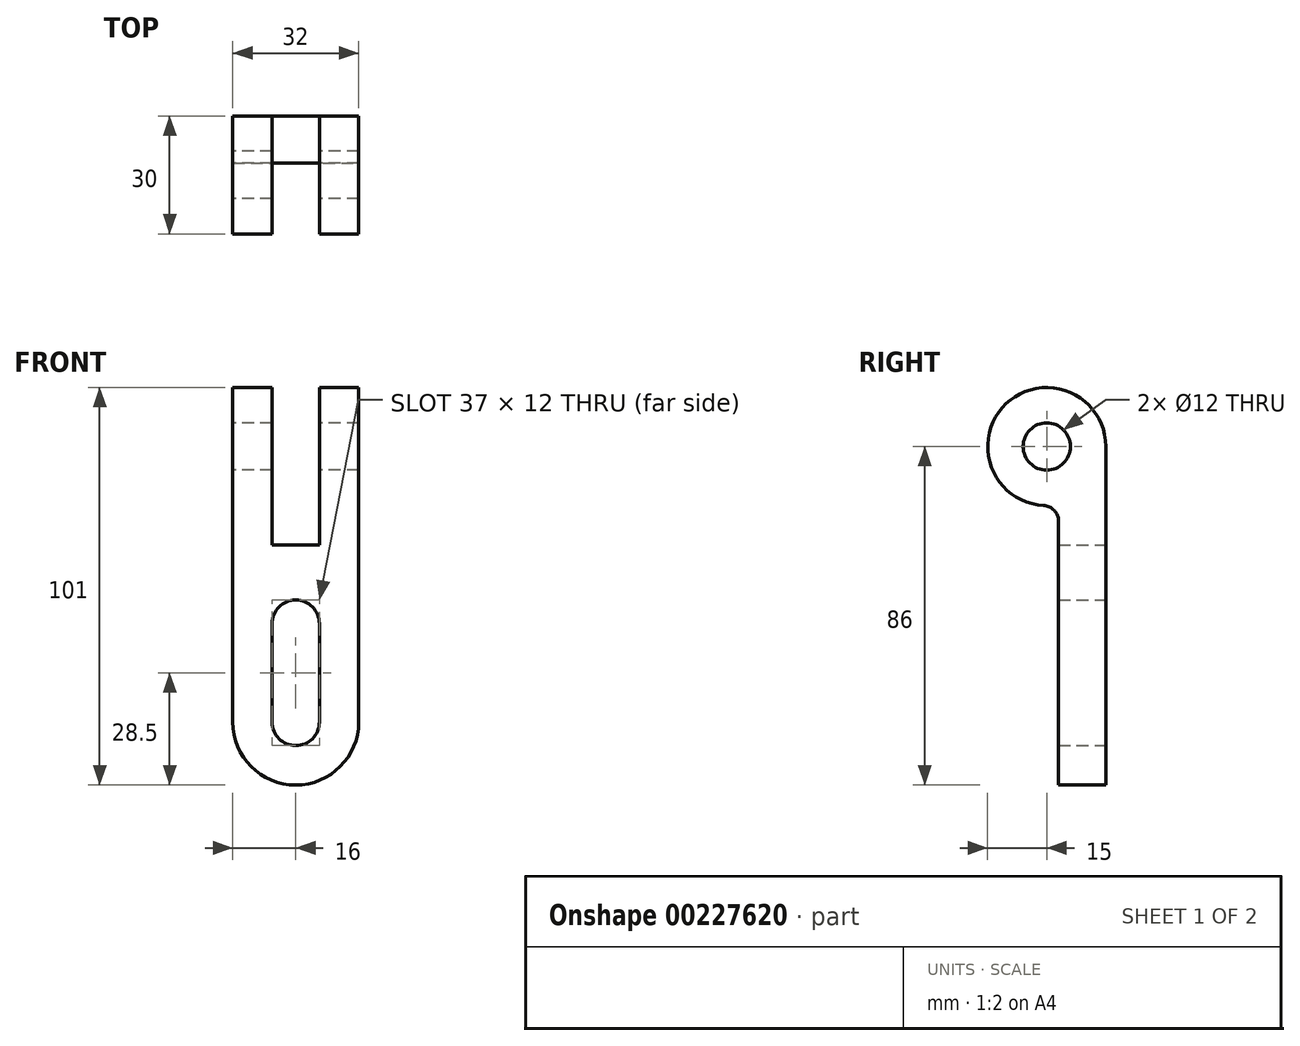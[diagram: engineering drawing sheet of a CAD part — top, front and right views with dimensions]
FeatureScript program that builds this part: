
annotation { "Feature Type Name" : "Feature", "Feature Type Description" : "" }
export const myFeature = defineFeature(function(context is Context, id is Id, definition is map)
    precondition{}
    {
        {
            var Q0;
            Q0=qCreatedBy(makeId("Right.planeOp"),FACE);
            var sketch = newSketch(context, id + "F0", { "sketchPlane" : qUnion([Q0])});
            skCircle(sketch, "E0", {"center": v(0, 0) * mm, "radius": 6 * mm});
            skArc(sketch, "E1", {"start": v(15, 0) * mm, "mid": v(-10.32, 10.88) * mm, "end": v(-0.79, -14.98) * mm});
            skLineSegment(sketch, "E2", {"start": v(3, -86) * mm, "end": v(15, -86) * mm});
            skLineSegment(sketch, "E3", {"start": v(15, -86) * mm, "end": v(15, 0) * mm});
            skLineSegment(sketch, "E4", {"start": v(3, -86) * mm, "end": v(3, -18.97) * mm});
            skPoint(sketch, "E5.visualSharp", {"position": v(3, -14.7) * mm});
            skArc(sketch, "E5.filletArc", {"start": v(3, -18.97) * mm, "mid": v(1.9, -16.22) * mm, "end": v(-0.79, -14.98) * mm});
            skSolve(sketch);
        }
        {
            var Q0;
            Q0 = qSketchRegion(id + "F0", true);
            extrude(context, id + "F1", {"entities" : qUnion([Q0]), "depth" : 16 * mm, "hasSecondDirection" : true, "secondDirectionOppositeDirection" : true, "secondDirectionDepth" : 16 * mm});
        }
        {
            var Q0;
            Q0=makeQuery(id+"F1.opExtrude","SWEPT_FACE",FACE,{"disambiguationData":[OSD([sQuery(id+"F0.wireOp",EDGE,"E3")])]});
            var sketch = newSketch(context, id + "F2", { "sketchPlane" : qUnion([Q0])});
            skLineSegment(sketch, "E6.bottom", {"start": v(-6, 18.67) * mm, "end": v(6, 18.67) * mm});
            skLineSegment(sketch, "E6.top", {"start": v(-6, -25) * mm, "end": v(6, -25) * mm});
            skLineSegment(sketch, "E6.left", {"start": v(-6, 18.67) * mm, "end": v(-6, -25) * mm});
            skLineSegment(sketch, "E6.right", {"start": v(6, 18.67) * mm, "end": v(6, -25) * mm});
            skLineSegment(sketch, "E7", {"start": v(-32.92, -70) * mm, "end": v(42.7, -70) * mm, "construction": true});
            skArc(sketch, "E8", {"start": v(6, -45) * mm, "mid": v(0, -39) * mm, "end": v(-6, -45) * mm});
            skArc(sketch, "E9", {"start": v(-6, -70) * mm, "mid": v(0, -76) * mm, "end": v(6, -70) * mm});
            skArc(sketch, "E10", {"start": v(-16, -70) * mm, "mid": v(0, -86) * mm, "end": v(16, -70) * mm});
            skLineSegment(sketch, "E11", {"start": v(-6, -45) * mm, "end": v(-6, -70) * mm});
            skLineSegment(sketch, "E12", {"start": v(6, -45) * mm, "end": v(6, -70) * mm});
            skSolve(sketch);
        }
        {
            var Q0;
            Q0 = qSketchRegion(id + "F2", true);
            var Q1;
            {var subQ0=sQuery(id+"F2.wireOp",EDGE,"E10");var subQ1=sQuery(id+"F0.wireOp",EDGE,"E3");var subQ2=makeQuery(id+"F1.opExtrude","CAP_EDGE",EDGE,{"disambiguationData":[OSD([subQ1])],"isStart":false});var subQ3=makeQuery(id+"F2.imprint","INTERSECT",VERTEX,{"derivedFrom":[subQ2,subQ0]});Q1=makeQuery(id+"F2.imprint","IMPRINT",FACE,{"disambiguationData":[TD([[makeQuery(id+"F2.imprint","IMPRINT",EDGE,{"disambiguationData":[TD([[subQ3,-1.0]])],"derivedFrom":subQ0}),-1.0]])]});}
            var Q2;
            {var subQ0=sQuery(id+"F2.wireOp",EDGE,"E10");var subQ1=sQuery(id+"F0.wireOp",EDGE,"E3");var subQ2=makeQuery(id+"F1.opExtrude","CAP_EDGE",EDGE,{"disambiguationData":[OSD([subQ1])],"isStart":true});var subQ3=makeQuery(id+"F2.imprint","INTERSECT",VERTEX,{"derivedFrom":[subQ2,subQ0]});Q2=makeQuery(id+"F2.imprint","IMPRINT",FACE,{"disambiguationData":[TD([[makeQuery(id+"F2.imprint","IMPRINT",EDGE,{"disambiguationData":[TD([[subQ3,1.0]])],"derivedFrom":subQ0}),-1.0]])]});}
            extrude(context, id + "F3", {"entities" : qUnion([Q0, Q1, Q2]), "operationType" : NewBodyOperationType.REMOVE, "endBound" : BoundingType.THROUGH_ALL, "oppositeDirection" : true, "depth" : 25 * mm});
        }
    });
